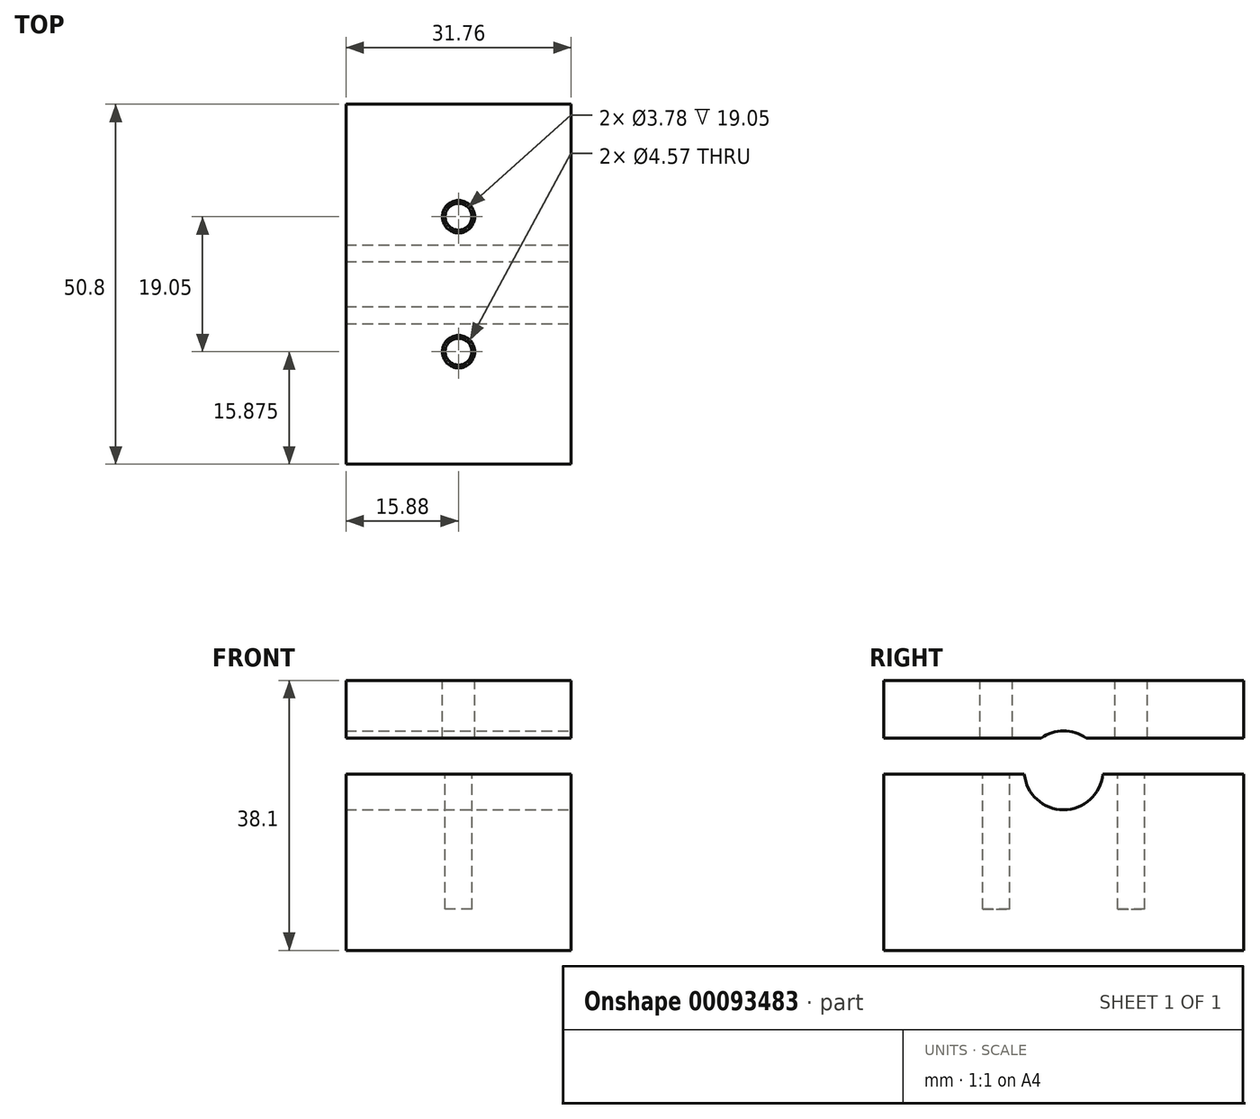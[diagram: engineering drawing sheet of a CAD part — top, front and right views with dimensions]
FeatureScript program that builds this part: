
annotation { "Feature Type Name" : "Feature", "Feature Type Description" : "" }
export const myFeature = defineFeature(function(context is Context, id is Id, definition is map)
    precondition{}
    {
        {
            var Q0;
            Q0=qCreatedBy(makeId("Top.planeOp"),FACE);
            var sketch = newSketch(context, id + "F0", { "sketchPlane" : qUnion([Q0])});
            skLineSegment(sketch, "E0.bottom", {"start": v(15.88, -25.4) * mm, "end": v(-15.87, -25.4) * mm});
            skLineSegment(sketch, "E0.top", {"start": v(15.88, 25.4) * mm, "end": v(-15.87, 25.4) * mm});
            skLineSegment(sketch, "E0.left", {"start": v(15.88, -25.4) * mm, "end": v(15.88, 25.4) * mm});
            skLineSegment(sketch, "E0.right", {"start": v(-15.87, -25.4) * mm, "end": v(-15.87, 25.4) * mm});
            skPoint(sketch, "E0.middle", {"position": v(0, 0) * mm});
            skSolve(sketch);
        }
        {
            var Q0;
            Q0 = qSketchRegion(id + "F0", true);
            extrude(context, id + "F1", {"entities" : qUnion([Q0]), "depth" : 38.1 * mm});
        }
        {
            var Q0;
            Q0=makeQuery(id+"F1.opExtrude","SWEPT_FACE",FACE,{"disambiguationData":[OSD([sQuery(id+"F0.wireOp",EDGE,"E0.left")])]});
            var sketch = newSketch(context, id + "F2", { "sketchPlane" : qUnion([Q0])});
            skArc(sketch, "E1", {"start": v(-5.54, 24.9) * mm, "mid": v(0, 19.84) * mm, "end": v(5.54, 24.9) * mm});
            skLineSegment(sketch, "E2.bottom", {"start": v(25.4, 29.97) * mm, "end": v(3.17, 29.97) * mm});
            skLineSegment(sketch, "E2.top", {"start": v(25.4, 24.9) * mm, "end": v(5.54, 24.9) * mm});
            skLineSegment(sketch, "E2.left", {"start": v(25.4, 29.97) * mm, "end": v(25.4, 24.9) * mm});
            skLineSegment(sketch, "E2.right", {"start": v(-25.4, 29.97) * mm, "end": v(-25.4, 24.9) * mm});
            skPoint(sketch, "E2.middle", {"position": v(0, 27.43) * mm});
            skArc(sketch, "E3.trimOffspring", {"start": v(3.17, 29.97) * mm, "mid": v(0, 30.96) * mm, "end": v(-3.17, 29.97) * mm});
            skLineSegment(sketch, "E4.trimOffspring", {"start": v(-5.54, 24.9) * mm, "end": v(-25.4, 24.9) * mm});
            skLineSegment(sketch, "E5.trimOffspring", {"start": v(-3.17, 29.97) * mm, "end": v(-25.4, 29.97) * mm});
            skSolve(sketch);
        }
        {
            var Q0;
            Q0 = qSketchRegion(id + "F2", true);
            extrude(context, id + "F3", {"entities" : qUnion([Q0]), "operationType" : NewBodyOperationType.REMOVE, "endBound" : BoundingType.THROUGH_ALL, "oppositeDirection" : true, "depth" : 25.4 * mm});
        }
        {
            var Q0;
            Q0=makeQuery(id+"F1.opExtrude","CAP_FACE",FACE,{"disambiguationData":[OSD([sQuery(id+"F0.wireOp",EDGE,"E0.bottom"),sQuery(id+"F0.wireOp",EDGE,"E0.top"),sQuery(id+"F0.wireOp",EDGE,"E0.left"),sQuery(id+"F0.wireOp",EDGE,"E0.right")])],"isStart":false});
            var sketch = newSketch(context, id + "F4", { "sketchPlane" : qUnion([Q0])});
            skCircle(sketch, "E6", {"center": v(0, 9.53) * mm, "radius": 2.29 * mm});
            skCircle(sketch, "E7", {"center": v(0, -9.53) * mm, "radius": 2.29 * mm});
            skSolve(sketch);
        }
        {
            var Q0;
            Q0 = qSketchRegion(id + "F4", true);
            extrude(context, id + "F5", {"entities" : qUnion([Q0]), "operationType" : NewBodyOperationType.REMOVE, "endBound" : BoundingType.UP_TO_NEXT, "oppositeDirection" : true, "depth" : 25.4 * mm});
        }
        {
            var Q0;
            Q0=makeQuery(id+"F3.boolean.opBoolean","COPY",FACE,{"derivedFrom":makeQuery(id+"F3.opExtrude","SWEPT_FACE",FACE,{"disambiguationData":[OSD([sQuery(id+"F2.wireOp",EDGE,"E2.top")])]})});
            var sketch = newSketch(context, id + "F6", { "sketchPlane" : qUnion([Q0])});
            skCircle(sketch, "E8", {"center": v(0, 9.53) * mm, "radius": 1.9 * mm});
            skCircle(sketch, "E9", {"center": v(0, -9.53) * mm, "radius": 1.9 * mm});
            skSolve(sketch);
        }
        {
            var Q0;
            Q0 = qSketchRegion(id + "F6", true);
            extrude(context, id + "F7", {"entities" : qUnion([Q0]), "operationType" : NewBodyOperationType.REMOVE, "oppositeDirection" : true, "depth" : 19.05 * mm});
        }
    });
